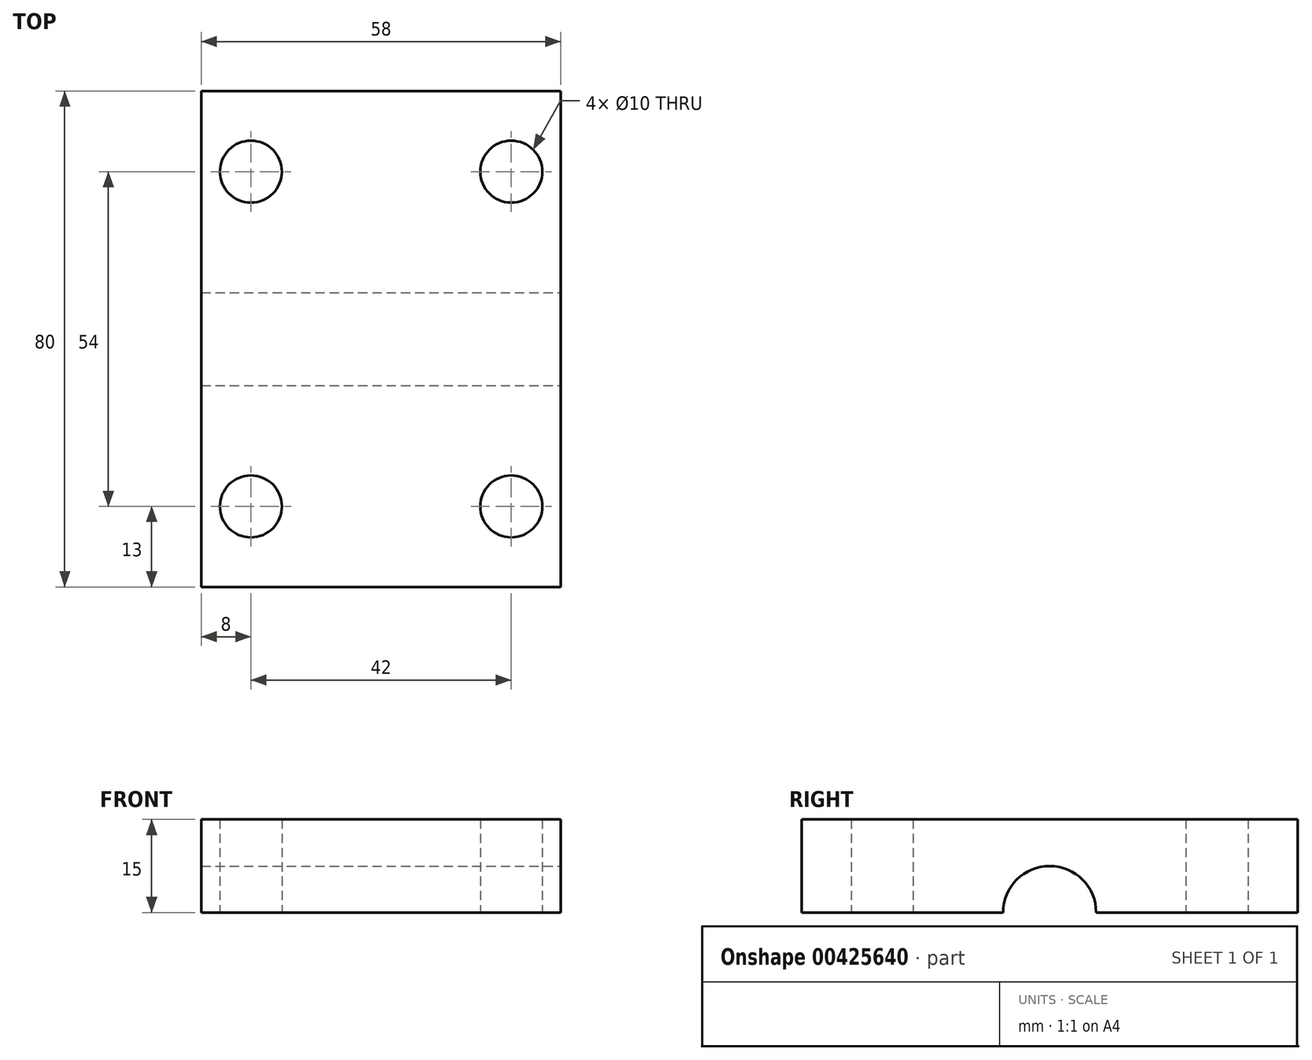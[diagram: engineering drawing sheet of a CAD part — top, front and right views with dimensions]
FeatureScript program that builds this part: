
annotation { "Feature Type Name" : "Feature", "Feature Type Description" : "" }
export const myFeature = defineFeature(function(context is Context, id is Id, definition is map)
    precondition{}
    {
        {
            var Q0;
            Q0=qCreatedBy(makeId("Top.planeOp"),FACE);
            var sketch = newSketch(context, id + "F0", { "sketchPlane" : qUnion([Q0])});
            skLineSegment(sketch, "E0.bottom", {"start": v(29, 40) * mm, "end": v(-29, 40) * mm});
            skLineSegment(sketch, "E0.top", {"start": v(29, -40) * mm, "end": v(-29, -40) * mm});
            skLineSegment(sketch, "E0.left", {"start": v(29, 40) * mm, "end": v(29, -40) * mm});
            skLineSegment(sketch, "E0.right", {"start": v(-29, 40) * mm, "end": v(-29, -40) * mm});
            skPoint(sketch, "E0.middle", {"position": v(0, 0) * mm});
            skLineSegment(sketch, "E1", {"start": v(0, 0) * mm, "end": v(0, 40) * mm, "construction": true});
            skLineSegment(sketch, "E2", {"start": v(0, 0) * mm, "end": v(-29, 0) * mm, "construction": true});
            skLineSegment(sketch, "E3", {"start": v(29, 0) * mm, "end": v(0, 0) * mm, "construction": true});
            skLineSegment(sketch, "E4", {"start": v(0, 0) * mm, "end": v(0, -40) * mm, "construction": true});
            skCircle(sketch, "E5", {"center": v(-21, 27) * mm, "radius": 5 * mm});
            skCircle(sketch, "E6.MirrorC", {"center": v(21, 27) * mm, "radius": 5 * mm});
            skLineSegment(sketch, "E7.MirrorCS", {"start": v(-29, 0) * mm, "end": v(0, 0) * mm, "construction": true});
            skCircle(sketch, "E8.MirrorC", {"center": v(21, -27) * mm, "radius": 5 * mm});
            skCircle(sketch, "E9.MirrorC", {"center": v(-21, -27) * mm, "radius": 5 * mm});
            skLineSegment(sketch, "E10.bottom", {"start": v(29, 7.5) * mm, "end": v(-29, 7.5) * mm});
            skLineSegment(sketch, "E10.top", {"start": v(29, -7.5) * mm, "end": v(-29, -7.5) * mm});
            skLineSegment(sketch, "E10.left", {"start": v(29, 7.5) * mm, "end": v(29, -7.5) * mm});
            skLineSegment(sketch, "E10.right", {"start": v(-29, 7.5) * mm, "end": v(-29, -7.5) * mm});
            skSolve(sketch);
        }
        {
            var Q0;
            {var subQ1=sQuery(id+"F0.wireOp",EDGE,"E0.bottom");Q0=makeQuery(id+"F0.imprint","IMPRINT",FACE,{"disambiguationData":[TD([[makeQuery(id+"F0.imprint","IMPRINT",EDGE,{"derivedFrom":subQ1}),1.0]])]});}
            var Q1;
            Q1=makeQuery(id+"F0.imprint","IMPRINT",FACE,{"disambiguationData":[TD([[makeQuery(id+"F0.imprint","IMPRINT",EDGE,{"derivedFrom":sQuery(id+"F0.wireOp",EDGE,"E10.bottom")}),1.0]])]});
            var Q2;
            {var subQ1=sQuery(id+"F0.wireOp",EDGE,"E0.top");Q2=makeQuery(id+"F0.imprint","IMPRINT",FACE,{"disambiguationData":[TD([[makeQuery(id+"F0.imprint","IMPRINT",EDGE,{"derivedFrom":subQ1}),-1.0]])]});}
            extrude(context, id + "F1", {"entities" : qUnion([Q0, Q1, Q2]), "depth" : 15 * mm});
        }
        {
            var Q0;
            Q0=qCreatedBy(makeId("Right.planeOp"),FACE);
            var sketch = newSketch(context, id + "F2", { "sketchPlane" : qUnion([Q0])});
            skCircle(sketch, "E11", {"center": v(0, 0) * mm, "radius": 7.5 * mm});
            skSolve(sketch);
        }
        {
            var Q0;
            Q0=makeQuery(id+"F2.imprint","IMPRINT",FACE,{"disambiguationData":[TD([[makeQuery(id+"F2.imprint","IMPRINT",EDGE,{"derivedFrom":sQuery(id+"F2.wireOp",EDGE,"E11")}),1.0]])]});
            var Q1;
            Q1=sQuery(id+"F2.wireOp",EDGE,"E11");
            extrude(context, id + "F3", {"entities" : qUnion([Q0]), "operationType" : NewBodyOperationType.REMOVE, "surfaceEntities" : qUnion([Q1]), "endBound" : BoundingType.SYMMETRIC, "oppositeDirection" : true, "depth" : 60 * mm});
        }
    });
